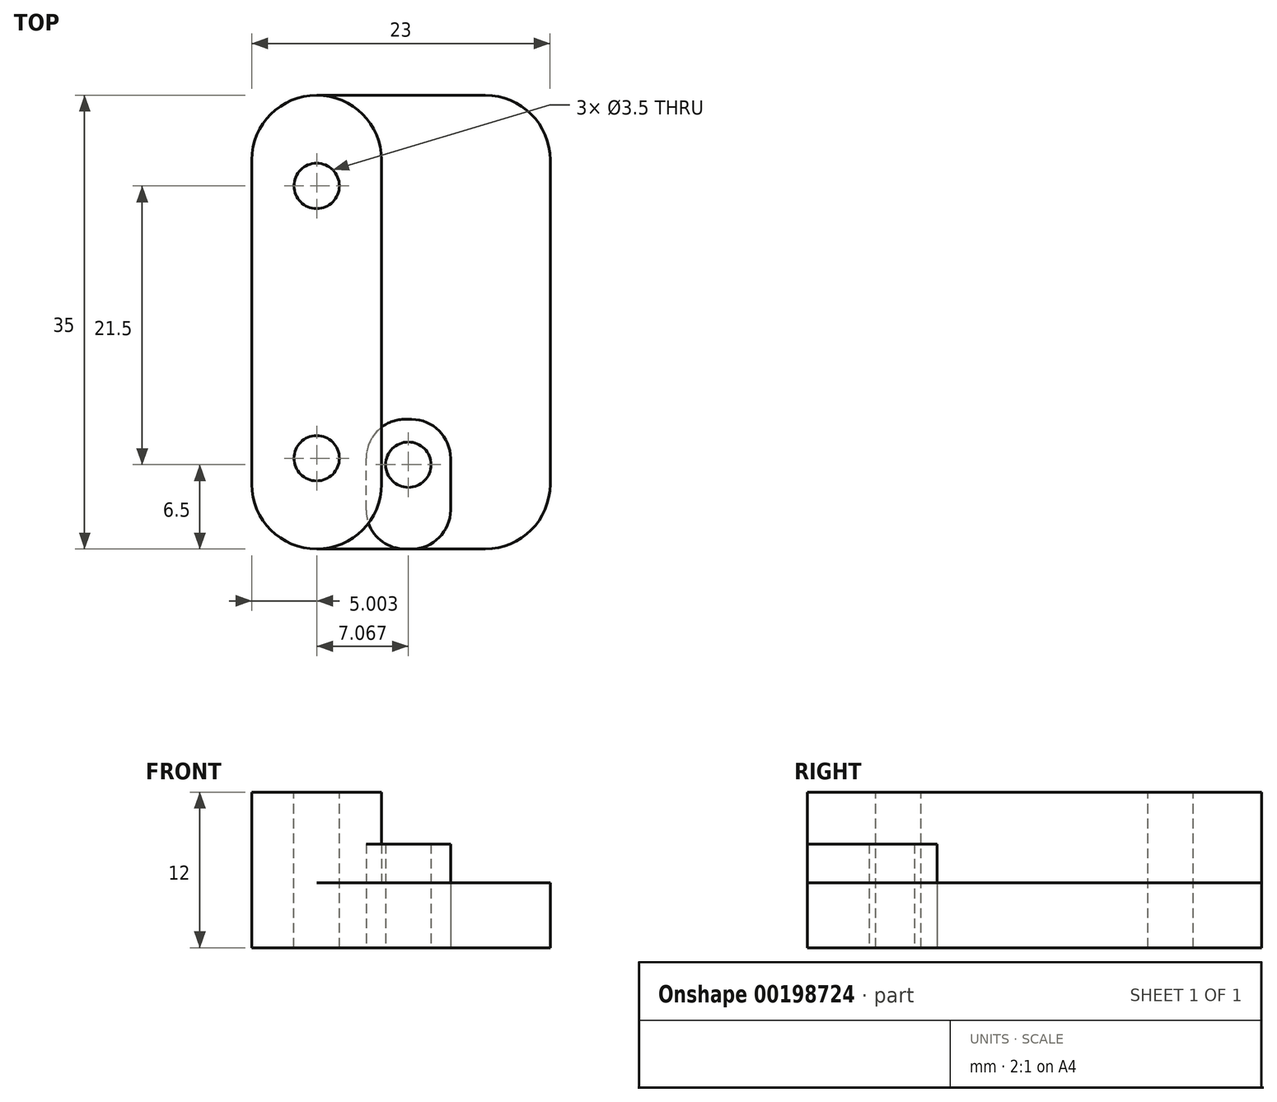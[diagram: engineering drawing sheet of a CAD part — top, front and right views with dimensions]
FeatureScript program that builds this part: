
annotation { "Feature Type Name" : "Feature", "Feature Type Description" : "" }
export const myFeature = defineFeature(function(context is Context, id is Id, definition is map)
    precondition{}
    {
        {
            var Q0;
            Q0=qCreatedBy(makeId("Top.planeOp"),FACE);
            var sketch = newSketch(context, id + "F0", { "sketchPlane" : qUnion([Q0])});
            skLineSegment(sketch, "E0.bottom", {"start": v(-8.82, 35) * mm, "end": v(14.18, 35) * mm});
            skLineSegment(sketch, "E0.top", {"start": v(-8.82, 0) * mm, "end": v(14.18, 0) * mm});
            skLineSegment(sketch, "E0.left", {"start": v(-8.82, 35) * mm, "end": v(-8.82, 0) * mm});
            skLineSegment(sketch, "E0.right", {"start": v(14.18, 35) * mm, "end": v(14.18, 0) * mm});
            skSolve(sketch);
        }
        {
            var Q0;
            Q0 = qSketchRegion(id + "F0", true);
            extrude(context, id + "F1", {"entities" : qUnion([Q0]), "depth" : 5 * mm, "offsetDistance" : 25 * mm});
        }
        {
            var Q0;
            Q0=makeQuery(id+"F1.opExtrude","CAP_FACE",FACE,{"disambiguationData":[OSD([sQuery(id+"F0.wireOp",EDGE,"E0.bottom"),sQuery(id+"F0.wireOp",EDGE,"E0.top"),sQuery(id+"F0.wireOp",EDGE,"E0.left"),sQuery(id+"F0.wireOp",EDGE,"E0.right")])],"isStart":false});
            var sketch = newSketch(context, id + "F2", { "sketchPlane" : qUnion([Q0])});
            skLineSegment(sketch, "E1.bottom", {"start": v(-8.82, 35) * mm, "end": v(1.18, 35) * mm});
            skLineSegment(sketch, "E1.top", {"start": v(-8.82, 0) * mm, "end": v(1.18, 0) * mm});
            skLineSegment(sketch, "E1.left", {"start": v(-8.82, 35) * mm, "end": v(-8.82, 0) * mm});
            skLineSegment(sketch, "E1.right", {"start": v(1.18, 35) * mm, "end": v(1.18, 0) * mm});
            skSolve(sketch);
        }
        {
            var Q0;
            Q0 = qSketchRegion(id + "F2", true);
            extrude(context, id + "F3", {"entities" : qUnion([Q0]), "operationType" : NewBodyOperationType.ADD, "depth" : 7 * mm, "offsetDistance" : 25 * mm});
        }
        {
            var Q0;
            Q0=makeQuery(id+"F3.opExtrude","CAP_FACE",FACE,{"disambiguationData":[OSD([sQuery(id+"F2.wireOp",EDGE,"E1.bottom"),sQuery(id+"F2.wireOp",EDGE,"E1.top"),sQuery(id+"F2.wireOp",EDGE,"E1.left"),sQuery(id+"F2.wireOp",EDGE,"E1.right")])],"isStart":false});
            var sketch = newSketch(context, id + "F4", { "sketchPlane" : qUnion([Q0])});
            skCircle(sketch, "E2", {"center": v(-3.82, 28) * mm, "radius": 1.75 * mm});
            skCircle(sketch, "E3", {"center": v(-3.82, 7) * mm, "radius": 1.75 * mm});
            skSolve(sketch);
        }
        {
            var Q0;
            Q0 = qSketchRegion(id + "F4", true);
            var Q1;
            Q1=makeQuery(id+"F1.opExtrude","CAP_FACE",FACE,{"disambiguationData":[OSD([sQuery(id+"F0.wireOp",EDGE,"E0.bottom"),sQuery(id+"F0.wireOp",EDGE,"E0.top"),sQuery(id+"F0.wireOp",EDGE,"E0.left"),sQuery(id+"F0.wireOp",EDGE,"E0.right")])],"isStart":true});
            extrude(context, id + "F5", {"entities" : qUnion([Q0]), "operationType" : NewBodyOperationType.REMOVE, "endBound" : BoundingType.UP_TO_SURFACE, "oppositeDirection" : true, "depth" : 25 * mm, "endBoundEntityFace" : qUnion([Q1]), "offsetDistance" : 25 * mm});
        }
        {
            var Q0;
            Q0=makeQuery(id+"F3.boolean.opBoolean","MERGE",EDGE,{"derivedFrom":[makeQuery(id+"F1.opExtrude","SWEPT_EDGE",EDGE,{"disambiguationData":[OSD([sQuery(id+"F0.wireOp",EDGE,"E0.bottom"),sQuery(id+"F0.wireOp",EDGE,"E0.left")])]}),makeQuery(id+"F3.opExtrude","SWEPT_EDGE",EDGE,{"disambiguationData":[OSD([sQuery(id+"F2.wireOp",EDGE,"E1.bottom"),sQuery(id+"F2.wireOp",EDGE,"E1.left")])]})]});
            var Q1;
            Q1=makeQuery(id+"F3.opExtrude","SWEPT_EDGE",EDGE,{"disambiguationData":[OSD([sQuery(id+"F0.wireOp",EDGE,"E0.bottom"),sQuery(id+"F2.wireOp",EDGE,"E1.bottom"),sQuery(id+"F2.wireOp",EDGE,"E1.right")])]});
            var Q2;
            Q2=makeQuery(id+"F3.boolean.opBoolean","MERGE",EDGE,{"derivedFrom":[makeQuery(id+"F1.opExtrude","SWEPT_EDGE",EDGE,{"disambiguationData":[OSD([sQuery(id+"F0.wireOp",EDGE,"E0.top"),sQuery(id+"F0.wireOp",EDGE,"E0.left")])]}),makeQuery(id+"F3.opExtrude","SWEPT_EDGE",EDGE,{"disambiguationData":[OSD([sQuery(id+"F2.wireOp",EDGE,"E1.top"),sQuery(id+"F2.wireOp",EDGE,"E1.left")])]})]});
            var Q3;
            Q3=makeQuery(id+"F3.opExtrude","SWEPT_EDGE",EDGE,{"disambiguationData":[OSD([sQuery(id+"F0.wireOp",EDGE,"E0.top"),sQuery(id+"F2.wireOp",EDGE,"E1.top"),sQuery(id+"F2.wireOp",EDGE,"E1.right")])]});
            var Q4;
            Q4=makeQuery(id+"F1.opExtrude","SWEPT_EDGE",EDGE,{"disambiguationData":[OSD([sQuery(id+"F0.wireOp",EDGE,"E0.top"),sQuery(id+"F0.wireOp",EDGE,"E0.right")])]});
            var Q5;
            Q5=makeQuery(id+"F1.opExtrude","SWEPT_EDGE",EDGE,{"disambiguationData":[OSD([sQuery(id+"F0.wireOp",EDGE,"E0.bottom"),sQuery(id+"F0.wireOp",EDGE,"E0.right")])]});
            fillet(context, id + "F6", {"entities" : qUnion([Q0, Q1, Q2, Q3, Q4, Q5]), "radius" : 5 * mm, "tangentPropagation" : true, "allowEdgeOverflow" : false});
        }
        {
            var Q0;
            Q0=qCreatedBy(makeId("Top.planeOp"),FACE);
            var sketch = newSketch(context, id + "F7", { "sketchPlane" : qUnion([Q0])});
            skLineSegment(sketch, "E4.bottom", {"start": v(0, 0) * mm, "end": v(6.5, 0) * mm});
            skLineSegment(sketch, "E4.top", {"start": v(0, 10) * mm, "end": v(6.5, 10) * mm});
            skLineSegment(sketch, "E4.left", {"start": v(0, 0) * mm, "end": v(0, 10) * mm});
            skLineSegment(sketch, "E4.right", {"start": v(6.5, 0) * mm, "end": v(6.5, 10) * mm});
            skCircle(sketch, "E5", {"center": v(3.25, 6.5) * mm, "radius": 1.75 * mm});
            skPoint(sketch, "E5.centerSnap0", {"position": v(3.25, 10) * mm});
            skSolve(sketch);
        }
        {
            var Q0;
            Q0 = qSketchRegion(id + "F7", true);
            extrude(context, id + "F8", {"entities" : qUnion([Q0]), "depth" : 8 * mm, "offsetDistance" : 25 * mm});
        }
        {
            var Q0;
            Q0=makeQuery(id+"F8.opExtrude","SWEPT_EDGE",EDGE,{"disambiguationData":[OSD([sQuery(id+"F7.wireOp",EDGE,"E4.bottom"),sQuery(id+"F7.wireOp",EDGE,"E4.right")])]});
            var Q1;
            Q1=makeQuery(id+"F8.opExtrude","SWEPT_EDGE",EDGE,{"disambiguationData":[OSD([sQuery(id+"F7.wireOp",EDGE,"E4.top"),sQuery(id+"F7.wireOp",EDGE,"E4.right")])]});
            var Q2;
            Q2=makeQuery(id+"F8.opExtrude","SWEPT_EDGE",EDGE,{"disambiguationData":[OSD([sQuery(id+"F7.wireOp",EDGE,"E4.bottom"),sQuery(id+"F7.wireOp",EDGE,"E4.left")])]});
            var Q3;
            Q3=makeQuery(id+"F8.opExtrude","SWEPT_EDGE",EDGE,{"disambiguationData":[OSD([sQuery(id+"F7.wireOp",EDGE,"E4.top"),sQuery(id+"F7.wireOp",EDGE,"E4.left")])]});
            fillet(context, id + "F9", {"entities" : qUnion([Q0, Q1, Q2, Q3]), "radius" : 3 * mm, "tangentPropagation" : true, "allowEdgeOverflow" : false});
        }
    });
